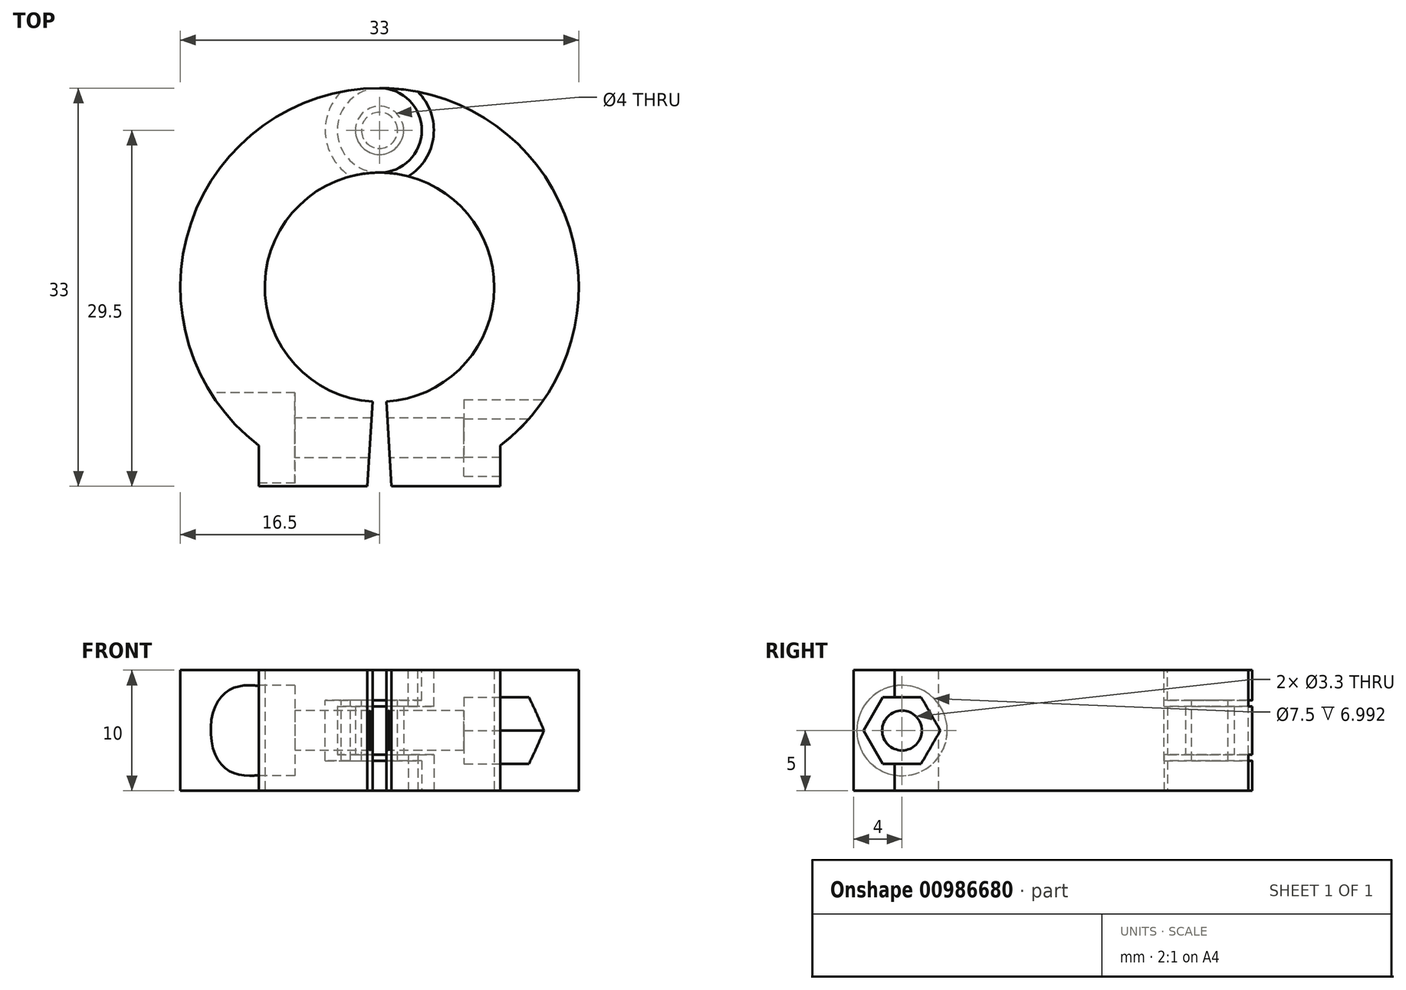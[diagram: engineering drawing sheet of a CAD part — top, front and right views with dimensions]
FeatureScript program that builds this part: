
annotation { "Feature Type Name" : "Feature", "Feature Type Description" : "" }
export const myFeature = defineFeature(function(context is Context, id is Id, definition is map)
    precondition{}
    {
        {
            var Q0;
            Q0=qCreatedBy(makeId("Top.planeOp"),FACE);
            var sketch = newSketch(context, id + "F0", { "sketchPlane" : qUnion([Q0])});
            skCircle(sketch, "E0", {"center": v(0, 0) * mm, "radius": 9.5 * mm});
            skCircle(sketch, "E1", {"center": v(0, 0) * mm, "radius": 16.5 * mm});
            skSolve(sketch);
        }
        {
            var Q0;
            Q0=makeQuery(id+"F0.imprint","IMPRINT",FACE,{"disambiguationData":[TD([[makeQuery(id+"F0.imprint","IMPRINT",EDGE,{"derivedFrom":sQuery(id+"F0.wireOp",EDGE,"xrZWLaRi-quKb-OQEF-ESTq-czxwHTAOTamJ")}),-1.0]])]});
            var Q1;
            Q1=makeQuery(id+"F0.imprint","IMPRINT",FACE,{"disambiguationData":[TD([[makeQuery(id+"F0.imprint","IMPRINT",EDGE,{"derivedFrom":sQuery(id+"F0.wireOp",EDGE,"E0")}),-1.0]])]});
            extrude(context, id + "F1", {"entities" : qUnion([Q0, Q1]), "depth" : 10 * mm, "offsetDistance" : 25 * mm});
        }
        {
            var Q0;
            Q0=makeQuery(id+"F1.opExtrude","CAP_FACE",FACE,{"disambiguationData":[OSD([sQuery(id+"F0.wireOp",EDGE,"E0"),sQuery(id+"F0.wireOp",EDGE,"E1")])],"isStart":false});
            var sketch = newSketch(context, id + "F2", { "sketchPlane" : qUnion([Q0])});
            skArc(sketch, "E2", {"start": v(0, 9.5) * mm, "mid": v(3.5, 13) * mm, "end": v(0, 16.5) * mm});
            skArc(sketch, "E3.0", {"start": v(0, 8.5) * mm, "mid": v(4.5, 13) * mm, "end": v(0, 17.5) * mm});
            skLineSegment(sketch, "E4", {"start": v(0, 17.5) * mm, "end": v(0, 16.5) * mm});
            skLineSegment(sketch, "E5", {"start": v(0, 9.5) * mm, "end": v(0, 8.5) * mm});
            skSolve(sketch);
        }
        {
            var Q0;
            Q0 = qSketchRegion(id + "F2", true);
            extrude(context, id + "F3", {"entities" : qUnion([Q0]), "operationType" : NewBodyOperationType.REMOVE, "oppositeDirection" : true, "depth" : 2.5 * mm, "offsetDistance" : 25 * mm});
        }
        {
            var Q0;
            Q0=makeQuery(id+"F3.boolean.opBoolean","COPY",FACE,{"derivedFrom":makeQuery(id+"F3.opExtrude","CAP_FACE",FACE,{"disambiguationData":[OSD([sQuery(id+"F2.wireOp",EDGE,"E2"),sQuery(id+"F2.wireOp",EDGE,"E3.0"),sQuery(id+"F2.wireOp",EDGE,"E4"),sQuery(id+"F2.wireOp",EDGE,"E5")])],"isStart":false})});
            var sketch = newSketch(context, id + "F4", { "sketchPlane" : qUnion([Q0])});
            skCircle(sketch, "E6", {"center": v(0, 13) * mm, "radius": 4.5 * mm});
            skCircle(sketch, "E7", {"center": v(0, 13) * mm, "radius": 1.5 * mm});
            skSolve(sketch);
        }
        {
            var Q0;
            Q0 = qSketchRegion(id + "F4", true);
            extrude(context, id + "F5", {"entities" : qUnion([Q0]), "operationType" : NewBodyOperationType.REMOVE, "oppositeDirection" : true, "depth" : 0.5 * mm, "offsetDistance" : 25 * mm});
        }
        {
            var Q0;
            Q0=makeQuery(id+"F1.opExtrude","CAP_FACE",FACE,{"disambiguationData":[OSD([sQuery(id+"F0.wireOp",EDGE,"E0"),sQuery(id+"F0.wireOp",EDGE,"E1")])],"isStart":true});
            var sketch = newSketch(context, id + "F6", { "sketchPlane" : qUnion([Q0])});
            skArc(sketch, "E8", {"start": v(0, -16.5) * mm, "mid": v(3.5, -13) * mm, "end": v(0, -9.5) * mm});
            skArc(sketch, "E9.0", {"start": v(0, -17.5) * mm, "mid": v(4.5, -13) * mm, "end": v(0, -8.5) * mm});
            skLineSegment(sketch, "E10", {"start": v(0, -8.5) * mm, "end": v(0, -9.5) * mm});
            skLineSegment(sketch, "E11", {"start": v(0, -17.5) * mm, "end": v(0, -16.5) * mm});
            skSolve(sketch);
        }
        {
            var Q0;
            Q0 = qSketchRegion(id + "F6", true);
            extrude(context, id + "F7", {"entities" : qUnion([Q0]), "operationType" : NewBodyOperationType.REMOVE, "oppositeDirection" : true, "depth" : 2.5 * mm, "offsetDistance" : 25 * mm});
        }
        {
            var Q0;
            Q0=makeQuery(id+"F7.boolean.opBoolean","COPY",FACE,{"derivedFrom":makeQuery(id+"F7.opExtrude","CAP_FACE",FACE,{"disambiguationData":[OSD([sQuery(id+"F6.wireOp",EDGE,"E8"),sQuery(id+"F6.wireOp",EDGE,"E9.0"),sQuery(id+"F6.wireOp",EDGE,"3cd00fd6-5b1b-43e5-87cb-27c4481d3068.0"),sQuery(id+"F6.wireOp",EDGE,"E11")])],"isStart":false})});
            var sketch = newSketch(context, id + "F8", { "sketchPlane" : qUnion([Q0])});
            skCircle(sketch, "E12", {"center": v(0, -13) * mm, "radius": 4.5 * mm});
            skCircle(sketch, "E13", {"center": v(0, -13) * mm, "radius": 1.5 * mm});
            skSolve(sketch);
        }
        {
            var Q0;
            Q0 = qSketchRegion(id + "F8", true);
            extrude(context, id + "F9", {"entities" : qUnion([Q0]), "operationType" : NewBodyOperationType.REMOVE, "oppositeDirection" : true, "depth" : 0.5 * mm, "offsetDistance" : 25 * mm});
        }
        {
            var Q0;
            Q0=makeQuery(id+"F9.boolean.opBoolean","COPY",FACE,{"derivedFrom":makeQuery(id+"F9.opExtrude","CAP_FACE",FACE,{"disambiguationData":[OSD([sQuery(id+"F8.wireOp",EDGE,"E12"),sQuery(id+"F8.wireOp",EDGE,"E13")])],"isStart":false})});
            var sketch = newSketch(context, id + "F10", { "sketchPlane" : qUnion([Q0])});
            skArc(sketch, "E14", {"start": v(0, -9.5) * mm, "mid": v(-3.5, -13) * mm, "end": v(0, -16.5) * mm});
            skArc(sketch, "E15.0", {"start": v(-2.4, -9.2) * mm, "mid": v(-4.47, -12.5) * mm, "end": v(-3.17, -16.2) * mm});
            skArc(sketch, "E16.0", {"start": v(-2.4, -9.2) * mm, "mid": v(-1.2, -9.42) * mm, "end": v(0, -9.5) * mm});
            skArc(sketch, "E17.0", {"start": v(-3.17, -16.2) * mm, "mid": v(-1.6, -16.42) * mm, "end": v(0, -16.5) * mm});
            skPoint(sketch, "E18.orphan", {"position": v(2.4, -9.2) * mm});
            skPoint(sketch, "E19.orphan", {"position": v(3.17, -16.2) * mm});
            skCircle(sketch, "E20", {"center": v(0, -13) * mm, "radius": 2 * mm});
            skCircle(sketch, "E21", {"center": v(0, -13) * mm, "radius": 1.5 * mm});
            skSolve(sketch);
        }
        {
            var Q0;
            Q0 = qSketchRegion(id + "F10", true);
            extrude(context, id + "F11", {"entities" : qUnion([Q0]), "operationType" : NewBodyOperationType.REMOVE, "endBound" : BoundingType.UP_TO_NEXT, "oppositeDirection" : true, "depth" : 25 * mm, "offsetDistance" : 25 * mm});
        }
        {
            var Q0;
            Q0=makeQuery(id+"F1.opExtrude","CAP_FACE",FACE,{"disambiguationData":[OSD([sQuery(id+"F0.wireOp",EDGE,"E0"),sQuery(id+"F0.wireOp",EDGE,"E1")])],"isStart":false});
            var sketch = newSketch(context, id + "F12", { "sketchPlane" : qUnion([Q0])});
            skLineSegment(sketch, "E22", {"start": v(-10, -16.5) * mm, "end": v(10, -16.5) * mm});
            skLineSegment(sketch, "E23", {"start": v(10, -16.5) * mm, "end": v(10, -13.12) * mm});
            skLineSegment(sketch, "E24", {"start": v(-10, -16.5) * mm, "end": v(-10, -13.12) * mm});
            skArc(sketch, "E25.0", {"start": v(-10, -13.12) * mm, "mid": v(0, -16.5) * mm, "end": v(10, -13.12) * mm});
            skSolve(sketch);
        }
        {
            var Q0;
            Q0 = qSketchRegion(id + "F12", true);
            var Q1;
            Q1=makeQuery(id+"F1.opExtrude","CAP_FACE",FACE,{"disambiguationData":[OSD([sQuery(id+"F0.wireOp",EDGE,"E0"),sQuery(id+"F0.wireOp",EDGE,"E1")])],"isStart":true});
            extrude(context, id + "F13", {"entities" : qUnion([Q0]), "operationType" : NewBodyOperationType.ADD, "endBound" : BoundingType.UP_TO_SURFACE, "oppositeDirection" : true, "depth" : 25 * mm, "endBoundEntityFace" : qUnion([Q1]), "offsetDistance" : 25 * mm});
        }
        {
            var Q0;
            Q0=makeQuery(id+"F13.boolean.opBoolean","MERGE",FACE,{"derivedFrom":[makeQuery(id+"F1.opExtrude","CAP_FACE",FACE,{"disambiguationData":[OSD([sQuery(id+"F0.wireOp",EDGE,"E0"),sQuery(id+"F0.wireOp",EDGE,"E1")])],"isStart":false}),makeQuery(id+"F13.opExtrude","CAP_FACE",FACE,{"disambiguationData":[OSD([sQuery(id+"F12.wireOp",EDGE,"E22"),sQuery(id+"F12.wireOp",EDGE,"E23"),sQuery(id+"F12.wireOp",EDGE,"E24"),sQuery(id+"F12.wireOp",EDGE,"E25.0")])],"isStart":true})]});
            var sketch = newSketch(context, id + "F14", { "sketchPlane" : qUnion([Q0])});
            skLineSegment(sketch, "E26", {"start": v(0, 0) * mm, "end": v(-1, -16.5) * mm});
            skLineSegment(sketch, "E27", {"start": v(-1, -16.5) * mm, "end": v(1, -16.5) * mm});
            skLineSegment(sketch, "E28", {"start": v(1, -16.5) * mm, "end": v(0, 0) * mm});
            skPoint(sketch, "E29", {"position": v(0, -16.5) * mm});
            skSolve(sketch);
        }
        {
            var Q0;
            Q0 = qSketchRegion(id + "F14", true);
            extrude(context, id + "F15", {"entities" : qUnion([Q0]), "operationType" : NewBodyOperationType.REMOVE, "endBound" : BoundingType.THROUGH_ALL, "oppositeDirection" : true, "depth" : 25 * mm, "offsetDistance" : 25 * mm});
        }
        {
            var Q0;
            Q0=makeQuery(id+"F13.opExtrude","SWEPT_FACE",FACE,{"disambiguationData":[OSD([sQuery(id+"F12.wireOp",EDGE,"E24")])]});
            var sketch = newSketch(context, id + "F16", { "sketchPlane" : qUnion([Q0])});
            skCircle(sketch, "E30", {"center": v(12.5, 5) * mm, "radius": 1.65 * mm});
            skSolve(sketch);
        }
        {
            var Q0;
            Q0 = qSketchRegion(id + "F16", true);
            var Q1;
            Q1=makeQuery(id+"F13.opExtrude","SWEPT_FACE",FACE,{"disambiguationData":[OSD([sQuery(id+"F12.wireOp",EDGE,"E23")])]});
            extrude(context, id + "F17", {"entities" : qUnion([Q0]), "operationType" : NewBodyOperationType.REMOVE, "endBound" : BoundingType.UP_TO_SURFACE, "oppositeDirection" : true, "depth" : 25 * mm, "endBoundEntityFace" : qUnion([Q1]), "offsetDistance" : 25 * mm});
        }
        {
            var Q0;
            Q0=makeQuery(id+"F13.opExtrude","SWEPT_FACE",FACE,{"disambiguationData":[OSD([sQuery(id+"F12.wireOp",EDGE,"E23")])]});
            var sketch = newSketch(context, id + "F18", { "sketchPlane" : qUnion([Q0])});
            skCircle(sketch, "E31.cCircle", {"center": v(-12.5, 5) * mm, "radius": 2.75 * mm, "construction": true});
            skLineSegment(sketch, "E31.0", {"start": v(-9.32, 5) * mm, "end": v(-10.91, 2.25) * mm});
            skLineSegment(sketch, "E31.1", {"start": v(-10.91, 2.25) * mm, "end": v(-14.09, 2.25) * mm});
            skLineSegment(sketch, "E31.2", {"start": v(-14.09, 2.25) * mm, "end": v(-15.68, 5) * mm});
            skLineSegment(sketch, "E31.3", {"start": v(-15.68, 5) * mm, "end": v(-14.09, 7.75) * mm});
            skLineSegment(sketch, "E31.4", {"start": v(-14.09, 7.75) * mm, "end": v(-10.91, 7.75) * mm});
            skLineSegment(sketch, "E31.5", {"start": v(-10.91, 7.75) * mm, "end": v(-9.32, 5) * mm});
            skPoint(sketch, "E31.0.midPoint", {"position": v(-10.12, 3.62) * mm});
            skSolve(sketch);
        }
        {
            var Q0;
            Q0 = qSketchRegion(id + "F18", true);
            extrude(context, id + "F19", {"entities" : qUnion([Q0]), "operationType" : NewBodyOperationType.REMOVE, "oppositeDirection" : true, "depth" : 3 * mm, "offsetDistance" : 25 * mm, "hasSecondDirection" : true, "secondDirectionOppositeDirection" : false, "secondDirectionDepth" : 10 * mm});
        }
        {
            var Q0;
            Q0=makeQuery(id+"F13.opExtrude","SWEPT_FACE",FACE,{"disambiguationData":[OSD([sQuery(id+"F12.wireOp",EDGE,"E24")])]});
            var sketch = newSketch(context, id + "F20", { "sketchPlane" : qUnion([Q0])});
            skCircle(sketch, "E32", {"center": v(12.5, 5) * mm, "radius": 3.75 * mm});
            skSolve(sketch);
        }
        {
            var Q0;
            Q0 = qSketchRegion(id + "F20", true);
            extrude(context, id + "F21", {"entities" : qUnion([Q0]), "operationType" : NewBodyOperationType.REMOVE, "oppositeDirection" : true, "depth" : 3 * mm, "offsetDistance" : 25 * mm, "hasSecondDirection" : true, "secondDirectionOppositeDirection" : false, "secondDirectionDepth" : 25 * mm});
        }
    });
